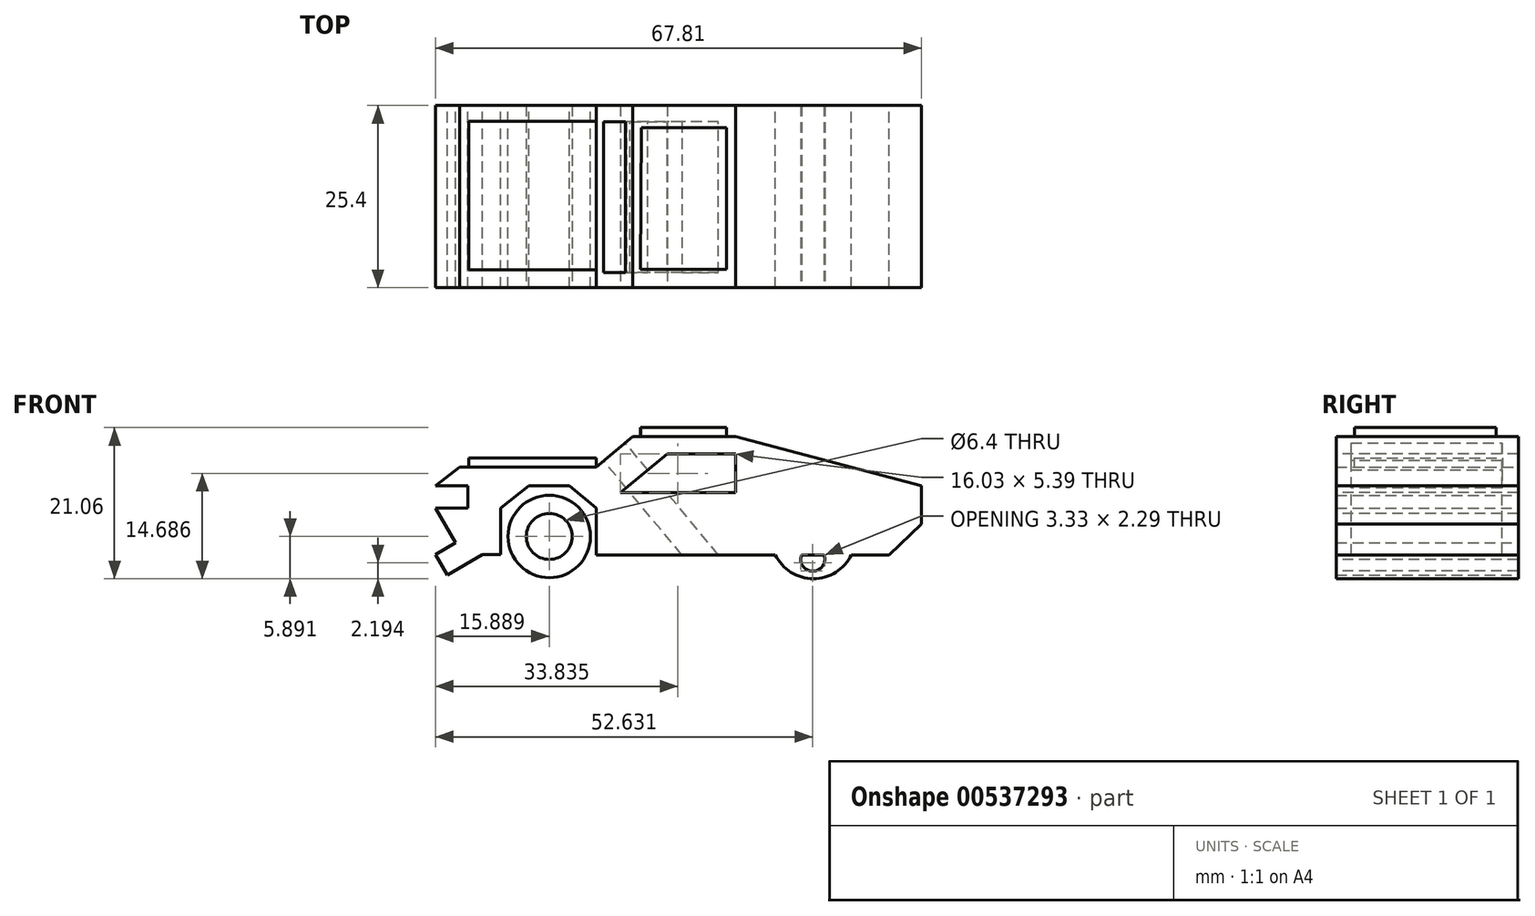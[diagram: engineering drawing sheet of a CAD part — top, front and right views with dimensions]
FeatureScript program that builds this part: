
annotation { "Feature Type Name" : "Feature", "Feature Type Description" : "" }
export const myFeature = defineFeature(function(context is Context, id is Id, definition is map)
    precondition{}
    {
        {
            var Q0;
            Q0=qCreatedBy(makeId("Front.planeOp"),FACE);
            var sketch = newSketch(context, id + "F0", { "sketchPlane" : qUnion([Q0])});
            skCircle(sketch, "E0", {"center": v(-25.96, 5.4) * mm, "radius": 5.74 * mm});
            skCircle(sketch, "E1", {"center": v(10.87, 5.4) * mm, "radius": 5.89 * mm});
            skSolve(sketch);
        }
        {
            var Q0;
            Q0=makeQuery(id+"F0.imprint","IMPRINT",FACE,{"disambiguationData":[TD([[makeQuery(id+"F0.imprint","IMPRINT",EDGE,{"derivedFrom":sQuery(id+"F0.wireOp",EDGE,"E0")}),1.0]])]});
            var Q1;
            Q1=makeQuery(id+"F0.imprint","IMPRINT",FACE,{"disambiguationData":[TD([[makeQuery(id+"F0.imprint","IMPRINT",EDGE,{"derivedFrom":sQuery(id+"F0.wireOp",EDGE,"E1")}),1.0]])]});
            extrude(context, id + "F1", {"entities" : qUnion([Q0, Q1]), "depth" : 25.4 * mm, "offsetDistance" : 25.4 * mm});
        }
        {
            var Q0;
            Q0=qCreatedBy(makeId("Front.planeOp"),FACE);
            var sketch = newSketch(context, id + "F2", { "sketchPlane" : qUnion([Q0])});
            skLineSegment(sketch, "E2", {"start": v(-19.44, 2.84) * mm, "end": v(21.42, 2.84) * mm});
            skLineSegment(sketch, "E3", {"start": v(21.42, 2.84) * mm, "end": v(25.96, 7.1) * mm});
            skLineSegment(sketch, "E4", {"start": v(25.96, 7.1) * mm, "end": v(25.96, 12.48) * mm});
            skLineSegment(sketch, "E5", {"start": v(25.96, 12.48) * mm, "end": v(0, 19.3) * mm});
            skLineSegment(sketch, "E6", {"start": v(0, 19.3) * mm, "end": v(-14.33, 19.3) * mm});
            skLineSegment(sketch, "E7", {"start": v(-14.33, 19.3) * mm, "end": v(-19.44, 15.04) * mm});
            skLineSegment(sketch, "E8", {"start": v(-19.44, 15.04) * mm, "end": v(-38.44, 15.04) * mm});
            skLineSegment(sketch, "E9", {"start": v(-38.44, 15.04) * mm, "end": v(-41.85, 12.48) * mm});
            skLineSegment(sketch, "E10", {"start": v(-41.85, 12.48) * mm, "end": v(-37.3, 12.48) * mm});
            skLineSegment(sketch, "E11", {"start": v(-37.3, 12.48) * mm, "end": v(-37.3, 9.36) * mm});
            skLineSegment(sketch, "E12", {"start": v(-37.3, 9.36) * mm, "end": v(-41.85, 9.36) * mm});
            skLineSegment(sketch, "E13", {"start": v(-41.85, 9.36) * mm, "end": v(-39.01, 4.54) * mm});
            skLineSegment(sketch, "E14", {"start": v(-39.01, 4.54) * mm, "end": v(-41.85, 2.87) * mm});
            skLineSegment(sketch, "E15", {"start": v(-41.85, 2.87) * mm, "end": v(-40.16, 0) * mm});
            skLineSegment(sketch, "E16", {"start": v(-40.16, 0) * mm, "end": v(-35.28, 2.87) * mm});
            skLineSegment(sketch, "E17", {"start": v(-35.28, 2.87) * mm, "end": v(-32.77, 2.87) * mm});
            skLineSegment(sketch, "E18", {"start": v(-32.77, 2.87) * mm, "end": v(-32.77, 9.36) * mm});
            skLineSegment(sketch, "E19", {"start": v(-32.77, 9.36) * mm, "end": v(-28.8, 12.48) * mm});
            skLineSegment(sketch, "E20", {"start": v(-28.8, 12.48) * mm, "end": v(-23.12, 12.48) * mm});
            skLineSegment(sketch, "E21", {"start": v(-23.12, 12.48) * mm, "end": v(-19.44, 9.36) * mm});
            skLineSegment(sketch, "E22", {"start": v(-19.44, 9.36) * mm, "end": v(-19.44, 2.84) * mm});
            skSolve(sketch);
        }
        {
            var Q0;
            Q0=qCreatedBy(makeId("Front.planeOp"),FACE);
            var sketch = newSketch(context, id + "F3", { "sketchPlane" : qUnion([Q0])});
            skLineSegment(sketch, "E23", {"start": v(-18.82, 12.03) * mm, "end": v(-13.9, 17.52) * mm});
            skLineSegment(sketch, "E24", {"start": v(-13.9, 17.52) * mm, "end": v(0, 17.52) * mm});
            skLineSegment(sketch, "E25", {"start": v(0, 17.52) * mm, "end": v(7.46, 14.05) * mm});
            skLineSegment(sketch, "E26", {"start": v(7.46, 14.05) * mm, "end": v(0, 11.74) * mm});
            skLineSegment(sketch, "E27", {"start": v(0, 11.74) * mm, "end": v(-18.82, 12.03) * mm});
            skSolve(sketch);
        }
        {
            var Q0;
            Q0=makeQuery(id+"F2.imprint","IMPRINT",FACE,{"disambiguationData":[TD([[makeQuery(id+"F2.imprint","IMPRINT",EDGE,{"derivedFrom":sQuery(id+"F2.wireOp",EDGE,"E2")}),1.0]])]});
            extrude(context, id + "F4", {"entities" : qUnion([Q0]), "operationType" : NewBodyOperationType.ADD, "depth" : 25.4 * mm, "offsetDistance" : 25.4 * mm});
        }
        {
            var Q0;
            Q0=makeQuery(id+"F3.imprint","IMPRINT",FACE,{"disambiguationData":[TD([[makeQuery(id+"F3.imprint","IMPRINT",EDGE,{"derivedFrom":sQuery(id+"F3.wireOp",EDGE,"E23")}),-1.0]])]});
            extrude(context, id + "F5", {"entities" : qUnion([Q0]), "operationType" : NewBodyOperationType.REMOVE, "oppositeDirection" : true, "depth" : 25.4 * mm, "offsetDistance" : 25.4 * mm});
        }
        {
            var Q0;
            Q0=makeQuery(id+"F1.opExtrude","CAP_FACE",FACE,{"disambiguationData":[OSD([sQuery(id+"F0.wireOp",EDGE,"E0")])],"isStart":false});
            var sketch = newSketch(context, id + "F6", { "sketchPlane" : qUnion([Q0])});
            skCircle(sketch, "E28", {"center": v(-25.96, 5.4) * mm, "radius": 3.2 * mm});
            skSolve(sketch);
        }
        {
            var Q0;
            Q0=makeQuery(id+"F6.imprint","IMPRINT",FACE,{"disambiguationData":[TD([[makeQuery(id+"F6.imprint","IMPRINT",EDGE,{"derivedFrom":sQuery(id+"F6.wireOp",EDGE,"E28")}),1.0]])]});
            extrude(context, id + "F7", {"entities" : qUnion([Q0]), "operationType" : NewBodyOperationType.REMOVE, "oppositeDirection" : true, "depth" : 25.4 * mm, "offsetDistance" : 25.4 * mm});
        }
        {
            var Q0;
            Q0=makeQuery(id+"F4.boolean.opBoolean","MERGE",FACE,{"derivedFrom":[makeQuery(id+"F1.opExtrude","CAP_FACE",FACE,{"disambiguationData":[OSD([sQuery(id+"F0.wireOp",EDGE,"E1")])],"isStart":false}),makeQuery(id+"F4.opExtrude","CAP_FACE",FACE,{"disambiguationData":[OSD([sQuery(id+"F2.wireOp",EDGE,"E2"),sQuery(id+"F2.wireOp",EDGE,"E3"),sQuery(id+"F2.wireOp",EDGE,"E4"),sQuery(id+"F2.wireOp",EDGE,"E5"),sQuery(id+"F2.wireOp",EDGE,"E6"),sQuery(id+"F2.wireOp",EDGE,"E7"),sQuery(id+"F2.wireOp",EDGE,"E8"),sQuery(id+"F2.wireOp",EDGE,"E9"),sQuery(id+"F2.wireOp",EDGE,"E10"),sQuery(id+"F2.wireOp",EDGE,"E11"),sQuery(id+"F2.wireOp",EDGE,"E12"),sQuery(id+"F2.wireOp",EDGE,"E13"),sQuery(id+"F2.wireOp",EDGE,"E14"),sQuery(id+"F2.wireOp",EDGE,"E15"),sQuery(id+"F2.wireOp",EDGE,"E16"),sQuery(id+"F2.wireOp",EDGE,"E17"),sQuery(id+"F2.wireOp",EDGE,"E18"),sQuery(id+"F2.wireOp",EDGE,"E19"),sQuery(id+"F2.wireOp",EDGE,"E20"),sQuery(id+"F2.wireOp",EDGE,"E21"),sQuery(id+"F2.wireOp",EDGE,"E22")])],"isStart":false})]});
            var sketch = newSketch(context, id + "F8", { "sketchPlane" : qUnion([Q0])});
            skLineSegment(sketch, "E29", {"start": v(9.22, 2.84) * mm, "end": v(12.34, 2.84) * mm});
            skArc(sketch, "E30", {"start": v(9.22, 2.84) * mm, "mid": v(10.78, 0.55) * mm, "end": v(12.34, 2.84) * mm});
            skSolve(sketch);
        }
        {
            var Q0;
            Q0=makeQuery(id+"F8.imprint","IMPRINT",FACE,{"disambiguationData":[TD([[makeQuery(id+"F8.imprint","IMPRINT",EDGE,{"derivedFrom":sQuery(id+"F8.wireOp",EDGE,"E29")}),-1.0]])]});
            extrude(context, id + "F9", {"entities" : qUnion([Q0]), "operationType" : NewBodyOperationType.REMOVE, "oppositeDirection" : true, "depth" : 25.4 * mm, "offsetDistance" : 25.4 * mm});
        }
        {
            var Q0;
            Q0=makeQuery(id+"F4.boolean.opBoolean","MERGE",FACE,{"derivedFrom":[makeQuery(id+"F1.opExtrude","CAP_FACE",FACE,{"disambiguationData":[OSD([sQuery(id+"F0.wireOp",EDGE,"E1")])],"isStart":false}),makeQuery(id+"F4.opExtrude","CAP_FACE",FACE,{"disambiguationData":[OSD([sQuery(id+"F2.wireOp",EDGE,"E2"),sQuery(id+"F2.wireOp",EDGE,"E3"),sQuery(id+"F2.wireOp",EDGE,"E4"),sQuery(id+"F2.wireOp",EDGE,"E5"),sQuery(id+"F2.wireOp",EDGE,"E6"),sQuery(id+"F2.wireOp",EDGE,"E7"),sQuery(id+"F2.wireOp",EDGE,"E8"),sQuery(id+"F2.wireOp",EDGE,"E9"),sQuery(id+"F2.wireOp",EDGE,"E10"),sQuery(id+"F2.wireOp",EDGE,"E11"),sQuery(id+"F2.wireOp",EDGE,"E12"),sQuery(id+"F2.wireOp",EDGE,"E13"),sQuery(id+"F2.wireOp",EDGE,"E14"),sQuery(id+"F2.wireOp",EDGE,"E15"),sQuery(id+"F2.wireOp",EDGE,"E16"),sQuery(id+"F2.wireOp",EDGE,"E17"),sQuery(id+"F2.wireOp",EDGE,"E18"),sQuery(id+"F2.wireOp",EDGE,"E19"),sQuery(id+"F2.wireOp",EDGE,"E20"),sQuery(id+"F2.wireOp",EDGE,"E21"),sQuery(id+"F2.wireOp",EDGE,"E22")])],"isStart":false})]});
            var sketch = newSketch(context, id + "F10", { "sketchPlane" : qUnion([Q0])});
            skLineSegment(sketch, "E31", {"start": v(-16.03, 11.5) * mm, "end": v(0, 11.5) * mm});
            skLineSegment(sketch, "E32", {"start": v(0, 11.5) * mm, "end": v(0, 16.88) * mm});
            skLineSegment(sketch, "E33", {"start": v(0, 16.88) * mm, "end": v(-9.5, 16.88) * mm});
            skLineSegment(sketch, "E34", {"start": v(-9.5, 16.88) * mm, "end": v(-16.03, 11.5) * mm});
            skSolve(sketch);
        }
        {
            var Q0;
            Q0=makeQuery(id+"F10.imprint","IMPRINT",FACE,{"disambiguationData":[TD([[makeQuery(id+"F10.imprint","IMPRINT",EDGE,{"derivedFrom":sQuery(id+"F10.wireOp",EDGE,"E31")}),1.0]])]});
            extrude(context, id + "F11", {"entities" : qUnion([Q0]), "operationType" : NewBodyOperationType.REMOVE, "oppositeDirection" : true, "depth" : 25.4 * mm, "offsetDistance" : 25.4 * mm});
        }
        {
            var Q0;
            Q0=makeQuery(id+"F4.opExtrude","SWEPT_FACE",FACE,{"disambiguationData":[OSD([sQuery(id+"F2.wireOp",EDGE,"E7")])]});
            var sketch = newSketch(context, id + "F12", { "sketchPlane" : qUnion([Q0])});
            skLineSegment(sketch, "E35", {"start": v(0, -2.27) * mm, "end": v(-3.92, -2.27) * mm});
            skLineSegment(sketch, "E36", {"start": v(-3.92, -2.27) * mm, "end": v(-3.92, -23.31) * mm});
            skLineSegment(sketch, "E37", {"start": v(-3.92, -23.31) * mm, "end": v(0, -23.31) * mm});
            skLineSegment(sketch, "E38", {"start": v(0, -23.31) * mm, "end": v(0, -2.27) * mm});
            skSolve(sketch);
        }
        {
            var Q0;
            Q0=makeQuery(id+"F12.imprint","IMPRINT",FACE,{"disambiguationData":[TD([[makeQuery(id+"F12.imprint","IMPRINT",EDGE,{"derivedFrom":sQuery(id+"F12.wireOp",EDGE,"E35")}),1.0]])]});
            extrude(context, id + "F13", {"entities" : qUnion([Q0]), "operationType" : NewBodyOperationType.REMOVE, "oppositeDirection" : true, "depth" : 25.4 * mm, "offsetDistance" : 25.4 * mm});
        }
        {
            var Q0;
            Q0=makeQuery(id+"F4.opExtrude","SWEPT_FACE",FACE,{"disambiguationData":[OSD([sQuery(id+"F2.wireOp",EDGE,"E6")])]});
            var sketch = newSketch(context, id + "F14", { "sketchPlane" : qUnion([Q0])});
            skLineSegment(sketch, "E39", {"start": v(-13.1, -3.06) * mm, "end": v(-1.24, -3.06) * mm});
            skLineSegment(sketch, "E40", {"start": v(-1.24, -3.06) * mm, "end": v(-1.24, -22.85) * mm});
            skLineSegment(sketch, "E41", {"start": v(-1.24, -22.85) * mm, "end": v(-13.22, -22.85) * mm});
            skLineSegment(sketch, "E42", {"start": v(-13.22, -22.85) * mm, "end": v(-13.1, -3.06) * mm});
            skSolve(sketch);
        }
        {
            var Q0;
            Q0=makeQuery(id+"F14.imprint","IMPRINT",FACE,{"disambiguationData":[TD([[makeQuery(id+"F14.imprint","IMPRINT",EDGE,{"derivedFrom":sQuery(id+"F14.wireOp",EDGE,"E39")}),-1.0]])]});
            extrude(context, id + "F15", {"entities" : qUnion([Q0]), "operationType" : NewBodyOperationType.ADD, "depth" : 27.94 * mm, "offsetDistance" : 25.4 * mm});
        }
        {
            var Q0;
            Q0=makeQuery(id+"F15.opExtrude","CAP_FACE",FACE,{"disambiguationData":[OSD([sQuery(id+"F14.wireOp",EDGE,"E39"),sQuery(id+"F14.wireOp",EDGE,"E40"),sQuery(id+"F14.wireOp",EDGE,"E41"),sQuery(id+"F14.wireOp",EDGE,"E42")])],"isStart":false});
            extrude(context, id + "F16", {"entities" : qUnion([Q0]), "operationType" : NewBodyOperationType.REMOVE, "oppositeDirection" : true, "depth" : 25.4 * mm, "offsetDistance" : 25.4 * mm});
        }
        {
            var Q0;
            Q0=makeQuery(id+"F16.boolean.opBoolean","COPY",FACE,{"derivedFrom":makeQuery(id+"F16.opExtrude","CAP_FACE",FACE,{"disambiguationData":[OSD([sQuery(id+"F14.wireOp",EDGE,"E39"),sQuery(id+"F14.wireOp",EDGE,"E40"),sQuery(id+"F14.wireOp",EDGE,"E41"),sQuery(id+"F14.wireOp",EDGE,"E42")])],"isStart":false})});
            extrude(context, id + "F17", {"entities" : qUnion([Q0]), "operationType" : NewBodyOperationType.REMOVE, "oppositeDirection" : true, "depth" : 1.27 * mm, "offsetDistance" : 25.4 * mm});
        }
        {
            var Q0;
            Q0=makeQuery(id+"F4.opExtrude","SWEPT_FACE",FACE,{"disambiguationData":[OSD([sQuery(id+"F2.wireOp",EDGE,"E8")])]});
            var sketch = newSketch(context, id + "F18", { "sketchPlane" : qUnion([Q0])});
            skLineSegment(sketch, "E43", {"start": v(-19.44, -22.92) * mm, "end": v(-37.17, -22.92) * mm});
            skLineSegment(sketch, "E44", {"start": v(-19.44, -22.92) * mm, "end": v(-19.44, -2.18) * mm});
            skLineSegment(sketch, "E45", {"start": v(-19.44, -2.18) * mm, "end": v(-37.17, -2.18) * mm});
            skLineSegment(sketch, "E46", {"start": v(-37.17, -2.18) * mm, "end": v(-37.17, -22.92) * mm});
            skSolve(sketch);
        }
        {
            var Q0;
            Q0=makeQuery(id+"F18.imprint","IMPRINT",FACE,{"disambiguationData":[TD([[makeQuery(id+"F18.imprint","IMPRINT",EDGE,{"derivedFrom":sQuery(id+"F18.wireOp",EDGE,"E43")}),-1.0]])]});
            extrude(context, id + "F19", {"entities" : qUnion([Q0]), "operationType" : NewBodyOperationType.ADD, "depth" : 2.54 * mm, "offsetDistance" : 25.4 * mm});
        }
        {
            var Q0;
            Q0=makeQuery(id+"F19.opExtrude","CAP_FACE",FACE,{"disambiguationData":[OSD([sQuery(id+"F18.wireOp",EDGE,"E43"),sQuery(id+"F18.wireOp",EDGE,"E44"),sQuery(id+"F18.wireOp",EDGE,"E45"),sQuery(id+"F18.wireOp",EDGE,"E46")])],"isStart":false});
            extrude(context, id + "F20", {"entities" : qUnion([Q0]), "operationType" : NewBodyOperationType.REMOVE, "oppositeDirection" : true, "depth" : 1.27 * mm, "offsetDistance" : 25.4 * mm});
        }
    });
